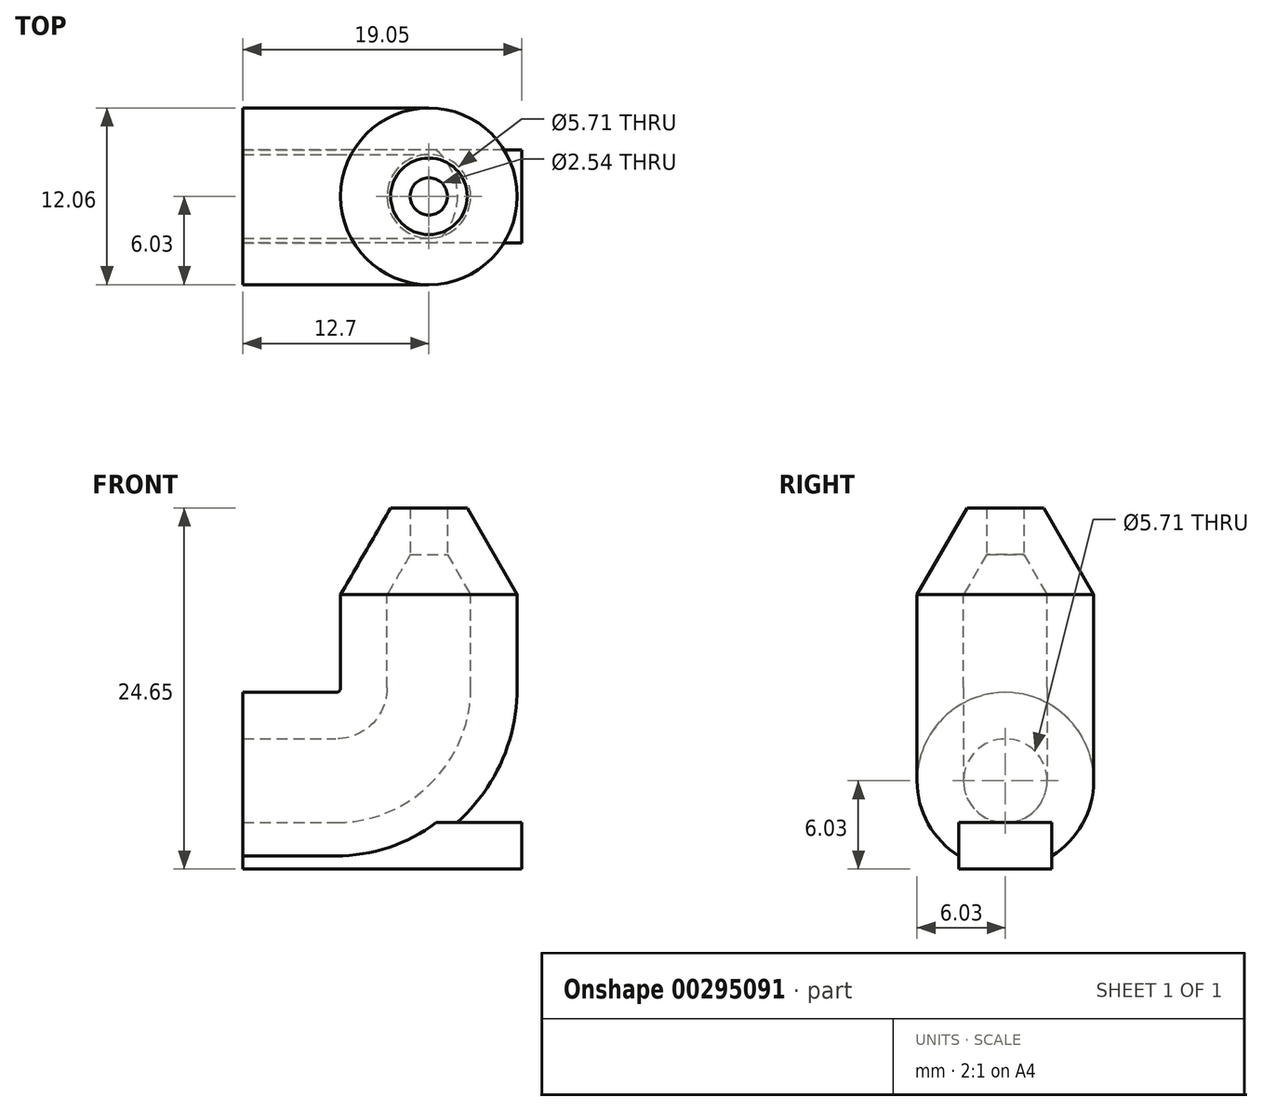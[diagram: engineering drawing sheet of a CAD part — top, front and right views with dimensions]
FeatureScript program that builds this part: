
annotation { "Feature Type Name" : "Feature", "Feature Type Description" : "" }
export const myFeature = defineFeature(function(context is Context, id is Id, definition is map)
    precondition{}
    {
        {
            var Q0;
            Q0=qCreatedBy(makeId("Right.planeOp"),FACE);
            var sketch = newSketch(context, id + "F0", { "sketchPlane" : qUnion([Q0])});
            skCircle(sketch, "E0", {"center": v(0, 0) * mm, "radius": 2.86 * mm});
            skCircle(sketch, "E1", {"center": v(0, 0) * mm, "radius": 6.03 * mm});
            skSolve(sketch);
        }
        {
            var Q0;
            Q0=qCreatedBy(makeId("Front.planeOp"),FACE);
            var sketch = newSketch(context, id + "F1", { "sketchPlane" : qUnion([Q0])});
            skLineSegment(sketch, "E2", {"start": v(0, 0) * mm, "end": v(6.35, 0) * mm});
            skLineSegment(sketch, "E3", {"start": v(12.7, 12.7) * mm, "end": v(12.7, 6.35) * mm});
            skPoint(sketch, "E4.visualSharp", {"position": v(12.7, 0) * mm});
            skArc(sketch, "E4.filletArc", {"start": v(6.35, 0) * mm, "mid": v(10.84, 1.86) * mm, "end": v(12.7, 6.35) * mm});
            skSolve(sketch);
        }
        {
            var Q0;
            Q0=makeQuery(id+"F0.imprint","IMPRINT",FACE,{"disambiguationData":[TD([[makeQuery(id+"F0.imprint","IMPRINT",EDGE,{"derivedFrom":sQuery(id+"F0.wireOp",EDGE,"E0")}),-1.0]])]});
            var Q1;
            Q1=sQuery(id+"F1.wireOp",EDGE,"E2");
            var Q2;
            Q2=sQuery(id+"F1.wireOp",EDGE,"E4.filletArc");
            var Q3;
            Q3=sQuery(id+"F1.wireOp",EDGE,"E3");
            sweep(context, id + "F2", {"profiles" : qUnion([Q0]), "path" : qUnion([Q1, Q2, Q3])});
        }
        {
            var Q0;
            Q0=qCreatedBy(makeId("Front.planeOp"),FACE);
            var sketch = newSketch(context, id + "F3", { "sketchPlane" : qUnion([Q0])});
            skLineSegment(sketch, "E5.0", {"start": v(9.84, 12.7) * mm, "end": v(15.56, 12.7) * mm});
            skLineSegment(sketch, "E6.0", {"start": v(6.67, 12.7) * mm, "end": v(18.73, 12.7) * mm});
            skLineSegment(sketch, "E7", {"start": v(12.7, 12.7) * mm, "end": v(12.7, 20.14) * mm});
            skLineSegment(sketch, "E8", {"start": v(9.84, 12.7) * mm, "end": v(11.43, 15.45) * mm});
            skLineSegment(sketch, "E9", {"start": v(11.43, 15.45) * mm, "end": v(11.43, 18.62) * mm});
            skLineSegment(sketch, "E10", {"start": v(11.43, 18.62) * mm, "end": v(10.09, 18.62) * mm});
            skLineSegment(sketch, "E11", {"start": v(10.09, 18.62) * mm, "end": v(6.67, 12.7) * mm});
            skSolve(sketch);
        }
        {
            var Q0;
            Q0 = qSketchRegion(id + "F3", true);
            var Q1;
            Q1=sQuery(id+"F3.wireOp",EDGE,"E7");
            revolve(context, id + "F4", {"operationType" : NewBodyOperationType.ADD, "entities" : qUnion([Q0]), "axis" : qUnion([Q1]), "revolveType" : RevolveType.FULL});
        }
        {
            var Q0;
            Q0=qCreatedBy(makeId("Right.planeOp"),FACE);
            var sketch = newSketch(context, id + "F5", { "sketchPlane" : qUnion([Q0])});
            skCircle(sketch, "E12.0", {"center": v(0, 0) * mm, "radius": 2.86 * mm});
            skCircle(sketch, "E13.0", {"center": v(0, 0) * mm, "radius": 6.03 * mm});
            skLineSegment(sketch, "E14", {"start": v(0, -2.86) * mm, "end": v(0, -6.03) * mm});
            skLineSegment(sketch, "E15.bottom", {"start": v(-3.18, -2.86) * mm, "end": v(3.18, -2.86) * mm});
            skLineSegment(sketch, "E15.top", {"start": v(-3.18, -6.03) * mm, "end": v(3.18, -6.03) * mm});
            skLineSegment(sketch, "E15.left", {"start": v(-3.18, -2.86) * mm, "end": v(-3.18, -6.03) * mm});
            skLineSegment(sketch, "E15.right", {"start": v(3.18, -2.86) * mm, "end": v(3.18, -6.03) * mm});
            skPoint(sketch, "E15.middle", {"position": v(0, -4.45) * mm});
            skSolve(sketch);
        }
        {
            var Q0;
            {var subQ0=sQuery(id+"F5.wireOp",EDGE,"E14");Q0=makeQuery(id+"F5.imprint","IMPRINT",FACE,{"disambiguationData":[TD([[makeQuery(id+"F5.imprint","IMPRINT",EDGE,{"derivedFrom":subQ0}),-1.0]])]});}
            var Q1;
            {var subQ0=sQuery(id+"F5.wireOp",EDGE,"E14");Q1=makeQuery(id+"F5.imprint","IMPRINT",FACE,{"disambiguationData":[TD([[makeQuery(id+"F5.imprint","IMPRINT",EDGE,{"derivedFrom":subQ0}),1.0]])]});}
            var Q2;
            {var subQ0=sQuery(id+"F5.wireOp",EDGE,"E15.top");var subQ3=sQuery(id+"F5.wireOp",EDGE,"E15.right");var subQ5=makeQuery(id+"F5.imprint","INTERSECT",VERTEX,{"derivedFrom":[subQ0,subQ3]});Q2=makeQuery(id+"F5.imprint","IMPRINT",FACE,{"disambiguationData":[TD([[makeQuery(id+"F5.imprint","IMPRINT",EDGE,{"disambiguationData":[TD([[subQ5,1.0]])],"derivedFrom":subQ3}),-1.0]])]});}
            var Q3;
            {var subQ0=sQuery(id+"F5.wireOp",EDGE,"E15.top");var subQ3=sQuery(id+"F5.wireOp",EDGE,"E15.left");var subQ5=makeQuery(id+"F5.imprint","INTERSECT",VERTEX,{"derivedFrom":[subQ0,subQ3]});Q3=makeQuery(id+"F5.imprint","IMPRINT",FACE,{"disambiguationData":[TD([[makeQuery(id+"F5.imprint","IMPRINT",EDGE,{"disambiguationData":[TD([[subQ5,1.0]])],"derivedFrom":subQ3}),1.0]])]});}
            extrude(context, id + "F6", {"entities" : qUnion([Q0, Q1, Q2, Q3]), "operationType" : NewBodyOperationType.ADD, "depth" : 19.05 * mm});
        }
    });
